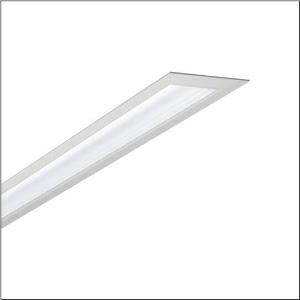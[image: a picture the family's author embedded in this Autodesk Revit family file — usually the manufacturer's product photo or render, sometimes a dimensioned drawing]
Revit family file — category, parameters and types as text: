
# Revit family: silica_r_5mx11dd1w4a_74f3
name_source: partatom
category: Lighting Fixtures
units: mm (PartAtom-declared; Revit-internal decimal feet)

## family parameters
Cut with Voids When Loaded = No
Host = Face
Light Source = No
Part Type = Normal
Room Calculation Point = No
Round Connector Dimension = Use Diameter
Shared = No

## types (1)
- --- (1 x LED, 3140 lm, 22.6 W, 4000K)
    Apparent Load = 23 VA
    CIE Flux Codes = 47 79 96 100 100
    Color Rendering = 80
    Color Temperature = 4000K
    Default Elevation = 1800 mm
    Description = Silica®, office luminaire, of aluminium, opal, light emission: direct distribution, primary light characteristic: symmetric, installation type: recessed, LED, rated luminous flux: 3.010lm, luminous efficacy: 123lm/W, light colour: 840, colour temperature: 4000K, control gear: DALI 2, with terminal, 3+2-pole, max. 2.5mm², mains connection: 230V, AC, 50/60Hz, rated input power: 24W, luminaire housing, of aluminium, matt pure white (RAL 9010), length: 1.462mm, width: 93mm, height: 60mm, end cap, of diecast zinc, pure white (RAL 9010), protection rating (complete): IP20, insulation class (complete): insulation class I (protective earthing), certification: CE, permissible operating ambient temperature: 0..+35°C, standard: EN 50419, packaging unit: 1 piece
    Height = 0 mm  [stored 0 ft]
    Lamp = 1 x LED
    Lamp Light Flux = 3140 lm
    Lamp Power = 22.6 W
    Lamp count = 1
    Length = 1462 mm
    Luminous efficacy = 139 lm/W
    Manufacturer = Siteco
    ModVariant = No
    Model = 5MX11DD1W4A
    Mounting Place = Ceiling
    Mounting Type = Recessed
    Number of Poles = 1
    OnlyDefault = Yes
    Power Factor = 1
    Product Name = Silica®
    Product group = office luminaire | ceiling recessed
    ProductGroupID = 401
    Protection Class = Protection class I
    Protection Degree = IP 20
    RLX_Detail_Level = 1
    RLX_Emergency_Light_Flux = 0 lm
    RLX_Emergency_Type = 0
    RLX_Emergency_Type_DB = No
    RlxData = <blob elided: 23873 chars, md5=6de9bfac>
    Socket = socket
    Standby Power = 0 W
    System Light Flux = 3140 lm
    System Power = 23 W
    Type Comments = factory setting: luminous flux: 100 % | dim-lin: 254 | 125 mA
    Type Image = l_1004825.jpg
    URL = http://relux.com
    VarID = @adj_197686
    Voltage = 0 V
    Weight = 0.00 kg
    Width = 93 mm

note: [stored X ft] marks values corroborated as IEEE doubles in the binary element streams (Revit-internal decimal feet)

## geometry (parser evidence)
native form markers: Blend x4, Sweep x10
no freeform markers — native parametric forms only
